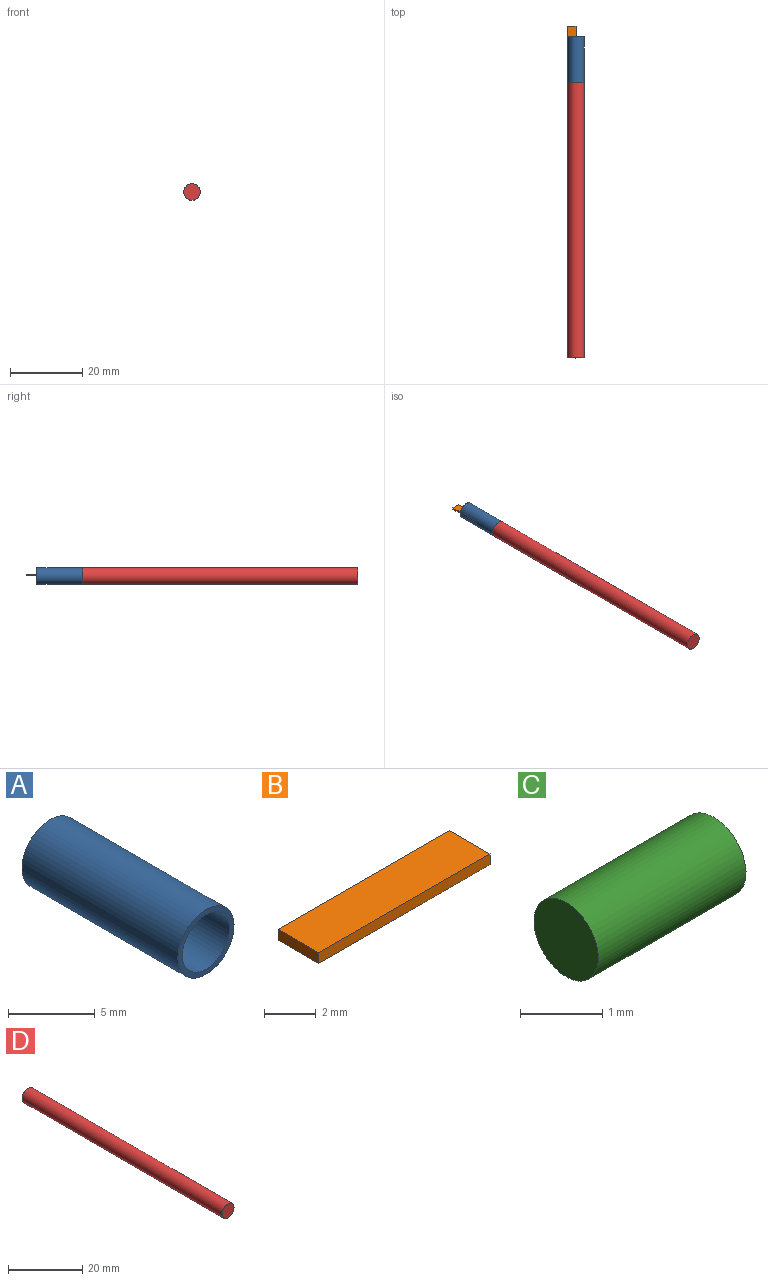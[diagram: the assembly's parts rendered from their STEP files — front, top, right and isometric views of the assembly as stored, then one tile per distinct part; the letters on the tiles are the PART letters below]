
ASSEMBLY  parts=4 mates=3
PART A: 5 faces, bbox 4.6x12.7x4.6 mm
  f0: cylinder r=2.29mm len=12.7mm, axis (0,1,0), area 182.4mm2, adj f1,f2
  f1: plane 4.57x4.57mm, normal (0,-1,0), area 4.9mm2, adj f0,f3
  f2: plane 4.57x4.57mm, normal (0,1,0), area 16.4mm2, adj f0
  f3: cylinder r=1.91mm len=8.89mm, axis (0,-1,0), area 106.9mm2, adj f1,f4
  f4: plane 3.83x3.83mm, normal (0,-1,0), area 11.5mm2, adj f3
PART B: 6 faces, bbox 9.3x2.2x0.5 mm
  f0: plane 9.34x0.51mm, normal (0,1,0), area 4.7mm2, adj f1,f3,f4,f5
  f1: plane 2.22x0.51mm, normal (-1,0,0), area 1.1mm2, adj f0,f2,f4,f5
  f2: plane 9.34x0.51mm, normal (0,-1,0), area 4.7mm2, adj f1,f3,f4,f5
  f3: plane 2.22x0.51mm, normal (1,0,0), area 1.1mm2, adj f0,f2,f4,f5
  f4: plane 9.34x2.22mm, normal (0,0,1), area 20.8mm2, adj f0,f1,f2,f3
  f5: plane 9.34x2.22mm, normal (0,0,-1), area 20.8mm2, adj f0,f1,f2,f3
PART C: 3 faces, bbox 2.5x1.1x1.1 mm
  f0: cylinder r=0.55mm len=2.54mm, axis (-1,0,0), area 8.8mm2, adj f1,f2
  f1: plane 1.11x1.11mm, normal (1,0,0), area 1mm2, adj f0
  f2: plane 1.11x1.11mm, normal (-1,0,0), area 1mm2, adj f0
PART D: 3 faces, bbox 4.6x76.2x4.6 mm
  f0: cylinder r=2.29mm len=76.2mm, axis (0,1,0), area 1095.3mm2, adj f1,f2
  f1: plane 4.58x4.58mm, normal (0,-1,0), area 16.4mm2, adj f0
  f2: plane 4.58x4.58mm, normal (0,1,0), area 16.4mm2, adj f0
PLACE A rot(axis=(0,1,0),0deg) t=(67.02,-12.46,49.3)mm
PLACE B rot(axis=(0,0,-1),90deg) t=(-4.97,-49.77,-9.03)mm
PLACE C rot(axis=(0.58,-0.58,-0.58),120deg) t=(-51.71,-22.62,-12.19)mm
PLACE D rot(axis=(0,1,0),0deg) t=(7.51,-25.16,-9.03)mm
MATE fastened C.f0 <-> D.f0  axis (0,1,0) through (7.51,-25.16,-9.03)mm
MATE fastened B.f3 <-> A.f0  axis (0,-1,0) through (7.51,-18.81,-9.03)mm
MATE slider D.f0 <-> A.f0  axis (0,1,0) through (7.51,-25.16,-9.03)mm
